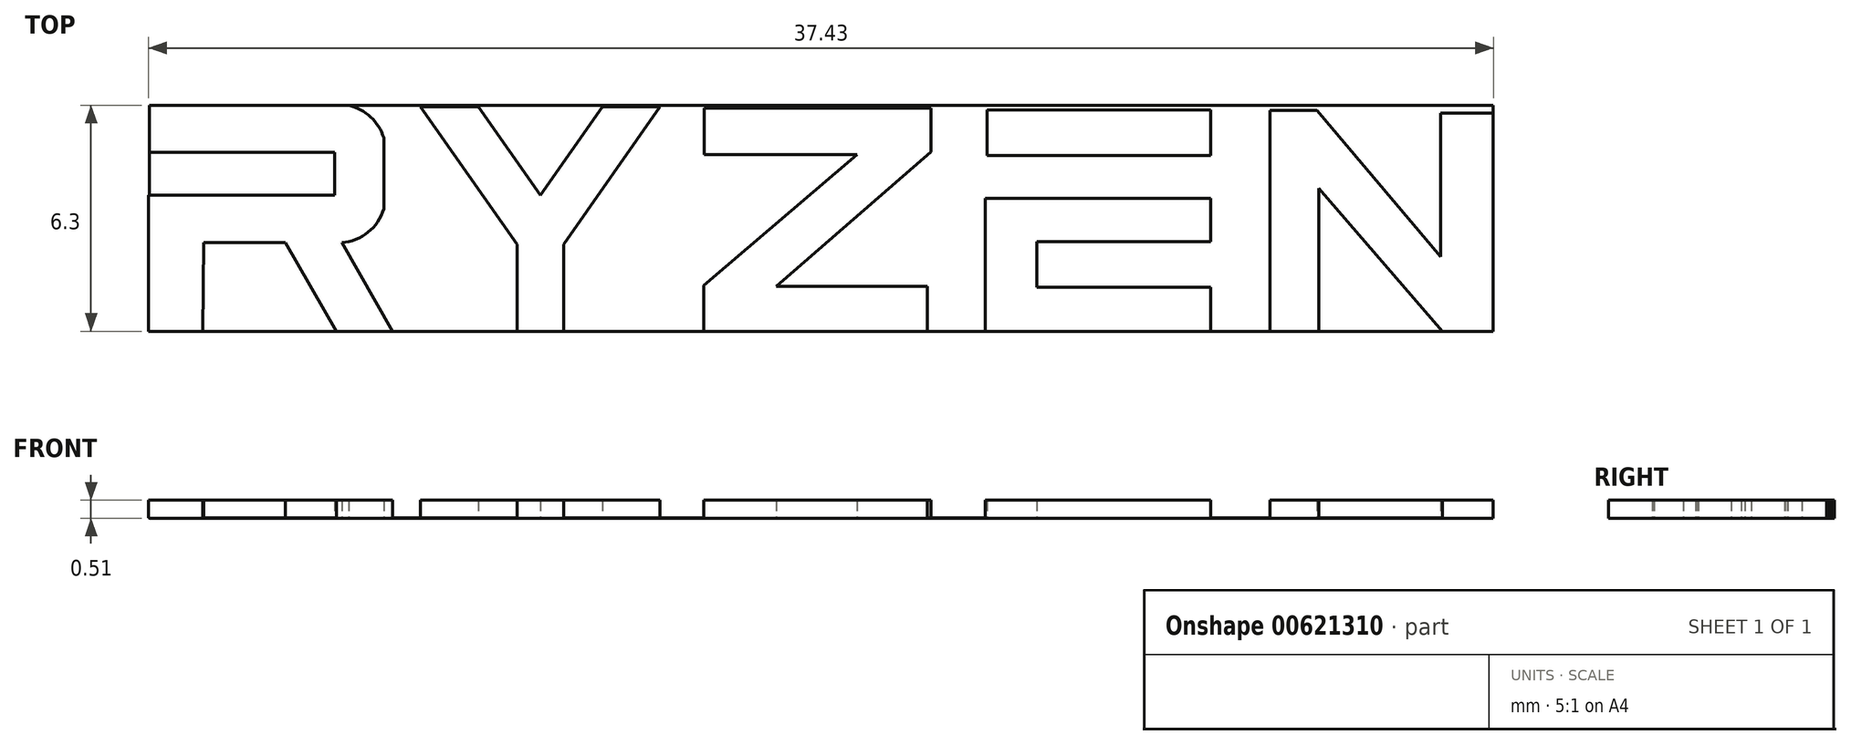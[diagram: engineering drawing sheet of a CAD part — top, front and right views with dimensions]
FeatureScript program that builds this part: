
annotation { "Feature Type Name" : "Feature", "Feature Type Description" : "" }
export const myFeature = defineFeature(function(context is Context, id is Id, definition is map)
    precondition{}
    {
        {
            assignVariable(context, id + "F0", {"name" : "scaling", "anyValue" : 0.5});
        }
        {
            assignVariable(context, id + "F1", {"name" : "TextHight", "anyValue" : 0.5});
        }
        {
            assignVariable(context, id + "F2", {"name" : "TextHightCalc", "anyValue" : getVariable(context, 'TextHight') / getVariable(context, 'scaling')});
        }
        {
            var Q0;
            Q0=qCreatedBy(makeId("Top.planeOp"),FACE);
            var sketch = newSketch(context, id + "F3", { "sketchPlane" : qUnion([Q0])});
            skLineSegment(sketch, "E0", {"start": v(-29.48, -7.6) * mm, "end": v(-32.5, -7.6) * mm});
            skLineSegment(sketch, "E1", {"start": v(-32.5, -7.6) * mm, "end": v(-32.5, 0) * mm});
            skLineSegment(sketch, "E2", {"start": v(-32.5, 0) * mm, "end": v(-22.16, 0) * mm});
            skLineSegment(sketch, "E3", {"start": v(-22.16, 0) * mm, "end": v(-22.16, 2.38) * mm});
            skLineSegment(sketch, "E4", {"start": v(-22.16, 2.38) * mm, "end": v(-32.47, 2.38) * mm});
            skLineSegment(sketch, "E5", {"start": v(-32.47, 2.38) * mm, "end": v(-32.47, 5) * mm});
            skLineSegment(sketch, "E6", {"start": v(-32.47, 5) * mm, "end": v(-21.36, 5) * mm});
            skLineSegment(sketch, "E7", {"start": v(-19.41, 3.18) * mm, "end": v(-19.41, -0.77) * mm});
            skLineSegment(sketch, "E8", {"start": v(-21.75, -2.65) * mm, "end": v(-18.91, -7.6) * mm});
            skLineSegment(sketch, "E9", {"start": v(-18.91, -7.6) * mm, "end": v(-22.04, -7.6) * mm});
            skLineSegment(sketch, "E10", {"start": v(-22.04, -7.6) * mm, "end": v(-24.88, -2.65) * mm});
            skLineSegment(sketch, "E11", {"start": v(-24.88, -2.65) * mm, "end": v(-29.43, -2.65) * mm});
            skLineSegment(sketch, "E12", {"start": v(-29.43, -2.65) * mm, "end": v(-29.48, -7.6) * mm});
            skLineSegment(sketch, "E13", {"start": v(-17.36, 4.92) * mm, "end": v(-12, -2.75) * mm});
            skLineSegment(sketch, "E14", {"start": v(-12, -2.75) * mm, "end": v(-12, -7.6) * mm});
            skLineSegment(sketch, "E15", {"start": v(-12, -7.6) * mm, "end": v(-9.4, -7.6) * mm});
            skLineSegment(sketch, "E16", {"start": v(-9.4, -7.6) * mm, "end": v(-9.4, -2.75) * mm});
            skLineSegment(sketch, "E17", {"start": v(-9.4, -2.75) * mm, "end": v(-4.03, 4.92) * mm});
            skLineSegment(sketch, "E18", {"start": v(-4.03, 4.92) * mm, "end": v(-7.25, 4.92) * mm});
            skLineSegment(sketch, "E19", {"start": v(-7.25, 4.92) * mm, "end": v(-10.7, 0) * mm});
            skLineSegment(sketch, "E20", {"start": v(-10.7, 0) * mm, "end": v(-14.14, 4.92) * mm});
            skLineSegment(sketch, "E21", {"start": v(-1.56, 2.24) * mm, "end": v(-1.56, 4.85) * mm});
            skLineSegment(sketch, "E22", {"start": v(-1.56, 4.85) * mm, "end": v(11.05, 4.85) * mm});
            skLineSegment(sketch, "E23", {"start": v(11.05, 4.85) * mm, "end": v(11.05, 2.4) * mm});
            skLineSegment(sketch, "E24", {"start": v(11.05, 2.4) * mm, "end": v(2.45, -5.08) * mm});
            skLineSegment(sketch, "E25", {"start": v(2.45, -5.08) * mm, "end": v(10.86, -5.08) * mm});
            skLineSegment(sketch, "E26", {"start": v(10.86, -5.08) * mm, "end": v(10.86, -7.6) * mm});
            skLineSegment(sketch, "E27", {"start": v(10.86, -7.6) * mm, "end": v(-1.6, -7.6) * mm});
            skLineSegment(sketch, "E28", {"start": v(-1.6, -7.6) * mm, "end": v(-1.6, -5.04) * mm});
            skLineSegment(sketch, "E29", {"start": v(-1.6, -5.04) * mm, "end": v(6.94, 2.24) * mm});
            skLineSegment(sketch, "E30", {"start": v(6.94, 2.24) * mm, "end": v(-1.56, 2.24) * mm});
            skLineSegment(sketch, "E31.bottom", {"start": v(14.18, 4.74) * mm, "end": v(26.63, 4.74) * mm});
            skLineSegment(sketch, "E31.top", {"start": v(14.18, 2.2) * mm, "end": v(26.63, 2.2) * mm});
            skLineSegment(sketch, "E31.left", {"start": v(14.18, 4.74) * mm, "end": v(14.18, 2.2) * mm});
            skLineSegment(sketch, "E31.right", {"start": v(26.63, 4.74) * mm, "end": v(26.63, 2.2) * mm});
            skLineSegment(sketch, "E32.bottom", {"start": v(26.63, -7.6) * mm, "end": v(14.09, -7.6) * mm});
            skLineSegment(sketch, "E32.top", {"start": v(26.63, -0.19) * mm, "end": v(14.09, -0.19) * mm});
            skLineSegment(sketch, "E32.right", {"start": v(14.09, -7.6) * mm, "end": v(14.09, -0.19) * mm});
            skLineSegment(sketch, "E33.bottom", {"start": v(16.94, -2.6) * mm, "end": v(26.63, -2.6) * mm});
            skLineSegment(sketch, "E33.top", {"start": v(16.94, -5.14) * mm, "end": v(26.63, -5.14) * mm});
            skLineSegment(sketch, "E33.left", {"start": v(16.94, -2.6) * mm, "end": v(16.94, -5.14) * mm});
            skLineSegment(sketch, "E34", {"start": v(26.63, -0.19) * mm, "end": v(26.63, -2.6) * mm});
            skLineSegment(sketch, "E35", {"start": v(26.63, -5.14) * mm, "end": v(26.63, -7.6) * mm});
            skLineSegment(sketch, "E36", {"start": v(32.65, -7.6) * mm, "end": v(29.91, -7.6) * mm});
            skLineSegment(sketch, "E37", {"start": v(29.91, -7.6) * mm, "end": v(29.91, 4.71) * mm});
            skLineSegment(sketch, "E38", {"start": v(29.91, 4.71) * mm, "end": v(32.54, 4.71) * mm});
            skLineSegment(sketch, "E39", {"start": v(32.54, 4.71) * mm, "end": v(39.43, -3.43) * mm});
            skLineSegment(sketch, "E40", {"start": v(39.43, -3.43) * mm, "end": v(39.43, 4.55) * mm});
            skLineSegment(sketch, "E41", {"start": v(39.43, 4.55) * mm, "end": v(42.36, 4.55) * mm});
            skLineSegment(sketch, "E42", {"start": v(42.36, 4.55) * mm, "end": v(42.36, -7.6) * mm});
            skLineSegment(sketch, "E43", {"start": v(42.36, -7.6) * mm, "end": v(39.52, -7.6) * mm});
            skLineSegment(sketch, "E44", {"start": v(39.52, -7.6) * mm, "end": v(32.65, 0.36) * mm});
            skLineSegment(sketch, "E45", {"start": v(32.65, 0.36) * mm, "end": v(32.65, -7.6) * mm});
            skArc(sketch, "E46", {"start": v(-19.41, 3.18) * mm, "mid": v(-20.15, 4.34) * mm, "end": v(-21.36, 5) * mm});
            skArc(sketch, "E47", {"start": v(-21.75, -2.65) * mm, "mid": v(-20.28, -2.08) * mm, "end": v(-19.41, -0.77) * mm});
            skLineSegment(sketch, "E48.bottom", {"start": v(-32.47, 5) * mm, "end": v(42.36, 5) * mm, "construction": true});
            skLineSegment(sketch, "E48.top", {"start": v(-32.47, -7.6) * mm, "end": v(42.36, -7.6) * mm, "construction": true});
            skLineSegment(sketch, "E48.left", {"start": v(-32.47, 5) * mm, "end": v(-32.47, -7.6) * mm, "construction": true});
            skLineSegment(sketch, "E48.right", {"start": v(42.36, 5) * mm, "end": v(42.36, -7.6) * mm, "construction": true});
            skLineSegment(sketch, "E49", {"start": v(-17.36, 4.92) * mm, "end": v(-14.14, 4.92) * mm});
            skSolve(sketch);
        }
        {
            var Q0;
            Q0 = qSketchRegion(id + "F3", true);
            extrude(context, id + "F4", {"entities" : qUnion([Q0]), "depth" : (getVariable(context, 'TextHightCalc')) * mm, "offsetDistance" : 25 * mm});
        }
        {
            var Q0;
            Q0=qCreatedBy(makeId("Top.planeOp"),FACE);
            var sketch = newSketch(context, id + "F5", { "sketchPlane" : qUnion([Q0])});
            skPoint(sketch, "E50.0", {"position": v(-32.47, 5) * mm});
            skPoint(sketch, "E51.0", {"position": v(42.36, -7.6) * mm});
            skLineSegment(sketch, "E52.bottom", {"start": v(-32.47, 5) * mm, "end": v(42.36, 5) * mm});
            skLineSegment(sketch, "E52.top", {"start": v(-32.47, -7.6) * mm, "end": v(42.36, -7.6) * mm});
            skLineSegment(sketch, "E52.left", {"start": v(-32.47, 5) * mm, "end": v(-32.47, -7.6) * mm});
            skLineSegment(sketch, "E52.right", {"start": v(42.36, 5) * mm, "end": v(42.36, -7.6) * mm});
            skSolve(sketch);
        }
        {
            var Q0;
            Q0=makeQuery(id+"F5.imprint","IMPRINT",FACE,{"disambiguationData":[TD([[makeQuery(id+"F5.imprint","IMPRINT",EDGE,{"derivedFrom":sQuery(id+"F5.wireOp",EDGE,"E52.bottom")}),-1.0]])]});
            extrude(context, id + "F6", {"entities" : qUnion([Q0]), "operationType" : NewBodyOperationType.ADD, "oppositeDirection" : true, "depth" : 0.01 * mm, "offsetDistance" : 25 * mm});
        }
        {
            var Q0;
            Q0=makeQuery(id+"F4.opExtrude","SWEPT_BODY",BODY,{"disambiguationData":[OSD([sQuery(id+"F3.wireOp",EDGE,"E32.bottom"),sQuery(id+"F3.wireOp",EDGE,"E32.top"),sQuery(id+"F3.wireOp",EDGE,"E32.right"),sQuery(id+"F3.wireOp",EDGE,"E33.bottom"),sQuery(id+"F3.wireOp",EDGE,"E33.top"),sQuery(id+"F3.wireOp",EDGE,"E33.left"),sQuery(id+"F3.wireOp",EDGE,"E34"),sQuery(id+"F3.wireOp",EDGE,"E35")])]});
            var Q1;
            Q1=makeQuery(id+"F4.opExtrude","SWEPT_BODY",BODY,{"disambiguationData":[OSD([sQuery(id+"F3.wireOp",EDGE,"E36"),sQuery(id+"F3.wireOp",EDGE,"E37"),sQuery(id+"F3.wireOp",EDGE,"E38"),sQuery(id+"F3.wireOp",EDGE,"E39"),sQuery(id+"F3.wireOp",EDGE,"E40"),sQuery(id+"F3.wireOp",EDGE,"E41"),sQuery(id+"F3.wireOp",EDGE,"E42"),sQuery(id+"F3.wireOp",EDGE,"E43"),sQuery(id+"F3.wireOp",EDGE,"E44"),sQuery(id+"F3.wireOp",EDGE,"E45")])]});
            var Q2;
            Q2=makeQuery(id+"F4.opExtrude","SWEPT_BODY",BODY,{"disambiguationData":[OSD([sQuery(id+"F3.wireOp",EDGE,"E0"),sQuery(id+"F3.wireOp",EDGE,"E1"),sQuery(id+"F3.wireOp",EDGE,"E2"),sQuery(id+"F3.wireOp",EDGE,"E3"),sQuery(id+"F3.wireOp",EDGE,"E4"),sQuery(id+"F3.wireOp",EDGE,"E5"),sQuery(id+"F3.wireOp",EDGE,"E6"),sQuery(id+"F3.wireOp",EDGE,"E7"),sQuery(id+"F3.wireOp",EDGE,"E8"),sQuery(id+"F3.wireOp",EDGE,"E9"),sQuery(id+"F3.wireOp",EDGE,"E10"),sQuery(id+"F3.wireOp",EDGE,"E11"),sQuery(id+"F3.wireOp",EDGE,"E12"),sQuery(id+"F3.wireOp",EDGE,"E46"),sQuery(id+"F3.wireOp",EDGE,"E47")])]});
            var Q3;
            Q3=makeQuery(id+"F4.opExtrude","SWEPT_BODY",BODY,{"disambiguationData":[OSD([sQuery(id+"F3.wireOp",EDGE,"E13"),sQuery(id+"F3.wireOp",EDGE,"E14"),sQuery(id+"F3.wireOp",EDGE,"E15"),sQuery(id+"F3.wireOp",EDGE,"E16"),sQuery(id+"F3.wireOp",EDGE,"E17"),sQuery(id+"F3.wireOp",EDGE,"E18"),sQuery(id+"F3.wireOp",EDGE,"E19"),sQuery(id+"F3.wireOp",EDGE,"E20"),sQuery(id+"F3.wireOp",EDGE,"E49")])]});
            var Q4;
            Q4=makeQuery(id+"F4.opExtrude","SWEPT_BODY",BODY,{"disambiguationData":[OSD([sQuery(id+"F3.wireOp",EDGE,"E21"),sQuery(id+"F3.wireOp",EDGE,"E22"),sQuery(id+"F3.wireOp",EDGE,"E23"),sQuery(id+"F3.wireOp",EDGE,"E24"),sQuery(id+"F3.wireOp",EDGE,"E25"),sQuery(id+"F3.wireOp",EDGE,"E26"),sQuery(id+"F3.wireOp",EDGE,"E27"),sQuery(id+"F3.wireOp",EDGE,"E28"),sQuery(id+"F3.wireOp",EDGE,"E29"),sQuery(id+"F3.wireOp",EDGE,"E30")])]});
            var Q5;
            Q5=makeQuery(id+"F4.opExtrude","SWEPT_BODY",BODY,{"disambiguationData":[OSD([sQuery(id+"F3.wireOp",EDGE,"E31.bottom"),sQuery(id+"F3.wireOp",EDGE,"E31.top"),sQuery(id+"F3.wireOp",EDGE,"E31.left"),sQuery(id+"F3.wireOp",EDGE,"E31.right")])]});
            var Q6;
            Q6=qCreatedBy(makeId("Origin.pointOp"),VERTEX);
            transform(context, id + "F7", {"entities" : qUnion([Q0, Q1, Q2, Q3, Q4, Q5]), "transformType" : TransformType.SCALE_UNIFORMLY, "scale" : getVariable(context, 'scaling'), "scalePoint" : qUnion([Q6]), "makeCopy" : false});
        }
    });
